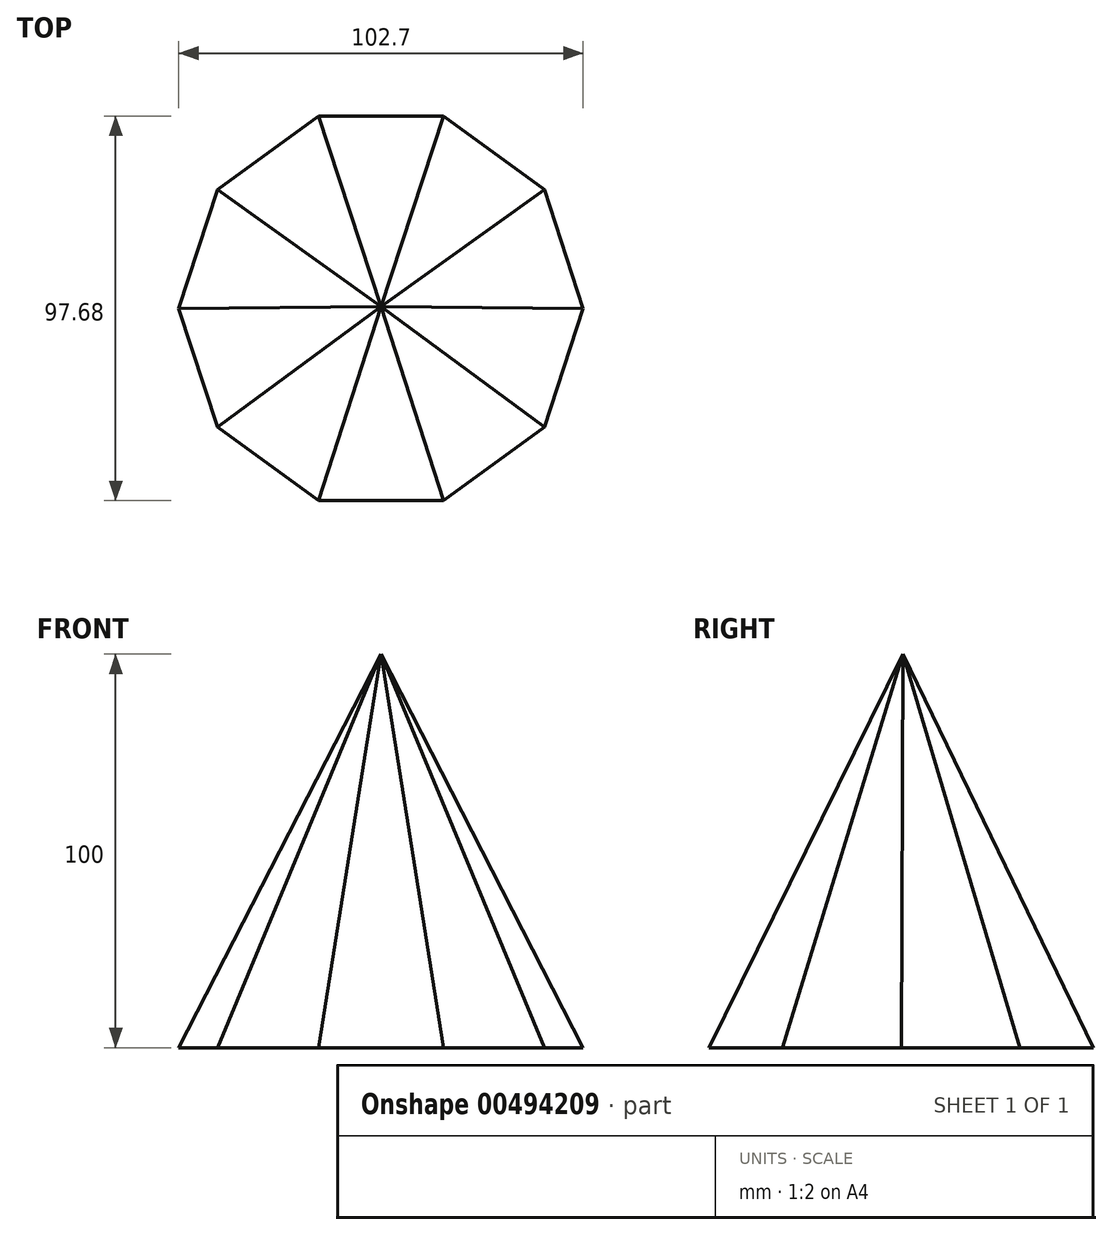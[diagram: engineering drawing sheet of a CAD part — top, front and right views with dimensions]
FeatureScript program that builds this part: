
annotation { "Feature Type Name" : "Feature", "Feature Type Description" : "" }
export const myFeature = defineFeature(function(context is Context, id is Id, definition is map)
    precondition{}
    {
        {
            var Q0;
            Q0=qCreatedBy(makeId("Top.planeOp"),FACE);
            var sketch = newSketch(context, id + "F0", { "sketchPlane" : qUnion([Q0])});
            skCircle(sketch, "E0.cCircle", {"center": v(0, 0) * mm, "radius": 51.35 * mm, "construction": true});
            skLineSegment(sketch, "E0.0", {"start": v(51.35, 0) * mm, "end": v(41.55, -30.18) * mm});
            skLineSegment(sketch, "E0.1", {"start": v(41.55, -30.18) * mm, "end": v(15.87, -48.84) * mm});
            skLineSegment(sketch, "E0.2", {"start": v(15.87, -48.84) * mm, "end": v(-15.87, -48.84) * mm});
            skLineSegment(sketch, "E0.3", {"start": v(-15.87, -48.84) * mm, "end": v(-41.55, -30.18) * mm});
            skLineSegment(sketch, "E0.4", {"start": v(-41.55, -30.18) * mm, "end": v(-51.35, 0) * mm});
            skLineSegment(sketch, "E0.5", {"start": v(-51.35, 0) * mm, "end": v(-41.55, 30.18) * mm});
            skLineSegment(sketch, "E0.6", {"start": v(-41.55, 30.18) * mm, "end": v(-15.87, 48.84) * mm});
            skLineSegment(sketch, "E0.7", {"start": v(-15.87, 48.84) * mm, "end": v(15.87, 48.84) * mm});
            skLineSegment(sketch, "E0.8", {"start": v(15.87, 48.84) * mm, "end": v(41.55, 30.18) * mm});
            skLineSegment(sketch, "E0.9", {"start": v(41.55, 30.18) * mm, "end": v(51.35, 0) * mm});
            skSolve(sketch);
        }
        {
            var Q0;
            Q0=qCreatedBy(makeId("Top.planeOp"),FACE);
            cPlane(context, id + "F1", {"entities" : qUnion([Q0]), "cplaneType" : CPlaneType.OFFSET, "offset" : 100 * mm, "width" : 150 * mm, "height" : 150 * mm});
        }
        {
            var Q0;
            Q0=qCreatedBy(id+"F1.planeOp",FACE);
            var sketch = newSketch(context, id + "F2", { "sketchPlane" : qUnion([Q0])});
            skPoint(sketch, "E1", {"position": v(0, 0.43) * mm});
            skSolve(sketch);
        }
        {
            var Q0;
            Q0=makeQuery(id+"F0.imprint","IMPRINT",FACE,{"disambiguationData":[TD([[makeQuery(id+"F0.imprint","IMPRINT",EDGE,{"derivedFrom":sQuery(id+"F0.wireOp",EDGE,"E0.0")}),-1.0]])]});
            var Q1;
            Q1=sQuery(id+"F2.wireOp",VERTEX,"E1");
            loft(context, id + "F3", {"sheetProfilesArray" : [{ "sheetProfileEntities" : qUnion([Q0]) }, { "sheetProfileEntities" : qUnion([Q1]) }]});
        }
    });
